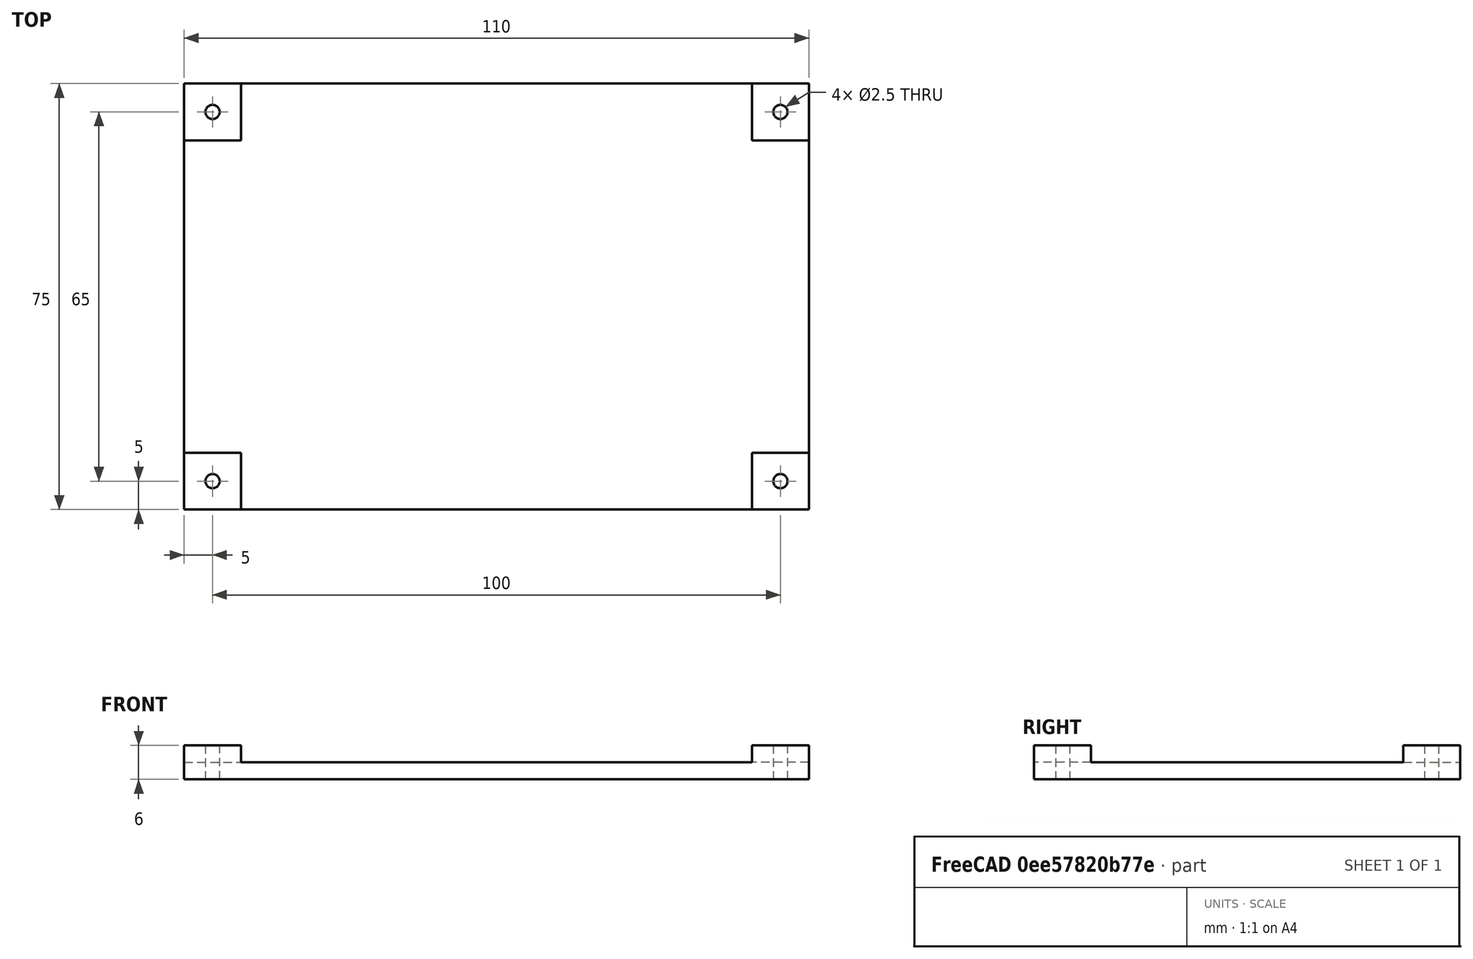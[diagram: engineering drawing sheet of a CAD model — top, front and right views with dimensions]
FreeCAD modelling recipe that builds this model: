
FCSTD DOCUMENT  (FreeCAD 0.20R29177 +233 (Git))
Label: Controller Mount Mk2
License: All rights reserved
LicenseURL: http://en.wikipedia.org/wiki/All_rights_reserved
objects: Part::Box×6, Part::Cylinder×4, Part::Cut×4, Part::MultiFuse×1, Part::Feature×1
note: 16 computed .brp shape members not serialized (recipe doc carries the construction recipe); baked Part::Feature solids carry a one-line shape summary decoded from their .brp

FEATURE [Part::Box] Box  label="Cube"
  AttacherType = Attacher::AttachEngine3D
  Height = 3
  Length = 110
  Width = 75
FEATURE [Part::Box] Box001  label="Cube001"
  AttacherType = Attacher::AttachEngine3D
  Height = 6
  Length = 10
  Width = 10
FEATURE [Part::Cylinder] Cylinder
  Angle = 360
  AttacherType = Attacher::AttachEngine3D
  FirstAngle = 0
  Height = 7
  Placement = pos=(5,5,-0.5) rot=(0,0,1;0rad)
  Radius = 1.25
  SecondAngle = 0
FEATURE [Part::Box] Box002  label="Cube002"
  AttacherType = Attacher::AttachEngine3D
  Height = 6
  Length = 10
  Placement = pos=(0,65,0) rot=(0,0,1;0rad)
  Width = 10
FEATURE [Part::Box] Box003  label="Cube003"
  AttacherType = Attacher::AttachEngine3D
  Height = 3
  Length = 110
  Width = 75
FEATURE [Part::Cylinder] Cylinder001
  Angle = 360
  AttacherType = Attacher::AttachEngine3D
  FirstAngle = 0
  Height = 7
  Placement = pos=(5,70,-0.5) rot=(0,0,1;0rad)
  Radius = 1.25
  SecondAngle = 0
FEATURE [Part::Box] Box004  label="Cube004"
  AttacherType = Attacher::AttachEngine3D
  Height = 6
  Length = 10
  Placement = pos=(100,65,0) rot=(0,0,1;0rad)
  Width = 10
FEATURE [Part::Cylinder] Cylinder002
  Angle = 360
  AttacherType = Attacher::AttachEngine3D
  FirstAngle = 0
  Height = 7
  Placement = pos=(105,70,-0.5) rot=(0,0,1;0rad)
  Radius = 1.25
  SecondAngle = 0
FEATURE [Part::Box] Box005  label="Cube005"
  AttacherType = Attacher::AttachEngine3D
  Height = 6
  Length = 10
  Placement = pos=(100,0,0) rot=(0,0,1;0rad)
  Width = 10
FEATURE [Part::Cylinder] Cylinder003
  Angle = 360
  AttacherType = Attacher::AttachEngine3D
  FirstAngle = 0
  Height = 7
  Placement = pos=(105,5,-0.5) rot=(0,0,1;0rad)
  Radius = 1.25
  SecondAngle = 0
FEATURE [Part::MultiFuse] Fusion
  Shapes = -> [Box,Box001,Box002,Box003,Box004,Box005]
FEATURE [Part::Feature] Fusion_solid  label="Fusion (Solid)"
  shape: bbox 110 x 75 x 6 mm, 38 faces (baked)
FEATURE [Part::Cut] Cut
  Base = -> Fusion_solid
  Tool = -> Cylinder003
FEATURE [Part::Cut] Cut001
  Base = -> Cut
  Tool = -> Cylinder002
FEATURE [Part::Cut] Cut002
  Base = -> Cut001
  Tool = -> Cylinder001
FEATURE [Part::Cut] Cut003
  Base = -> Cut002
  Tool = -> Cylinder
